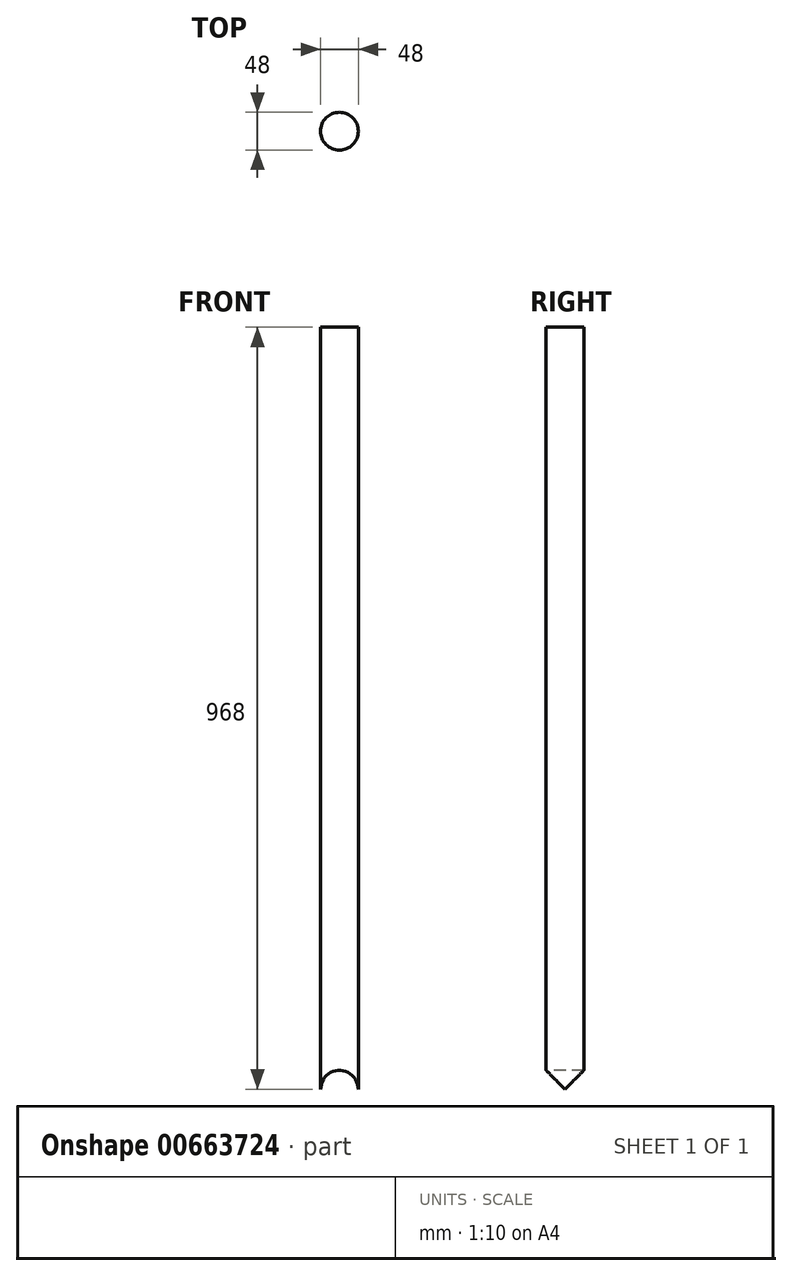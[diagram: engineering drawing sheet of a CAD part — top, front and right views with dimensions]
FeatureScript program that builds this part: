
annotation { "Feature Type Name" : "Feature", "Feature Type Description" : "" }
export const myFeature = defineFeature(function(context is Context, id is Id, definition is map)
    precondition{}
    {
        {
            var Q0;
            Q0=qCreatedBy(makeId("Top.planeOp"),FACE);
            var sketch = newSketch(context, id + "F0", { "sketchPlane" : qUnion([Q0])});
            skCircle(sketch, "E0", {"center": v(0, 0) * mm, "radius": 24 * mm});
            skSolve(sketch);
        }
        {
            var Q0;
            Q0=makeQuery(id+"F0.imprint","IMPRINT",FACE,{"disambiguationData":[TD([[makeQuery(id+"F0.imprint","IMPRINT",EDGE,{"derivedFrom":sQuery(id+"F0.wireOp",EDGE,"E0")}),1.0]])]});
            extrude(context, id + "F1", {"entities" : qUnion([Q0]), "depth" : (1000 - 2 - 24 - 6) * mm, "offsetDistance" : 25 * mm});
        }
        {
            var Q0;
            Q0=qCreatedBy(makeId("Front.planeOp"),FACE);
            var sketch = newSketch(context, id + "F2", { "sketchPlane" : qUnion([Q0])});
            skCircle(sketch, "E1", {"center": v(0, 0) * mm, "radius": 24 * mm});
            skSolve(sketch);
        }
        {
            var Q0;
            Q0 = qSketchRegion(id + "F2", true);
            extrude(context, id + "F3", {"entities" : qUnion([Q0]), "operationType" : NewBodyOperationType.REMOVE, "endBound" : BoundingType.SYMMETRIC, "oppositeDirection" : true, "depth" : 100 * mm, "offsetDistance" : 25 * mm});
        }
    });
